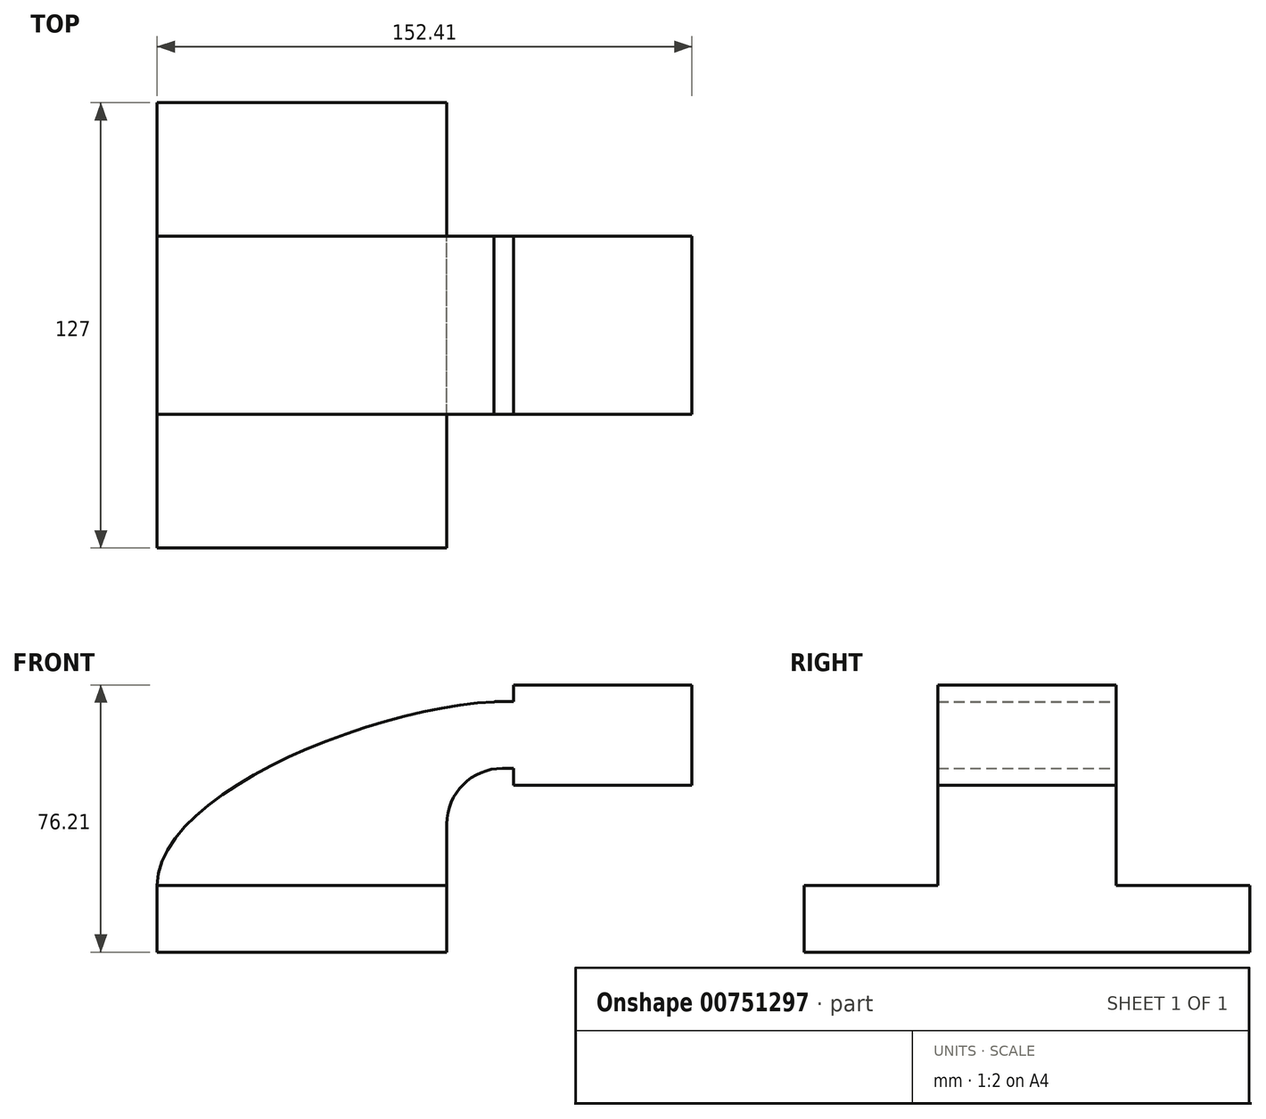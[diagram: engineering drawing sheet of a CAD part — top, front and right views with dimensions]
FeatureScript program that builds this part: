
annotation { "Feature Type Name" : "Feature", "Feature Type Description" : "" }
export const myFeature = defineFeature(function(context is Context, id is Id, definition is map)
    precondition{}
    {
        {
            var Q0;
            Q0=qCreatedBy(makeId("Front.planeOp"),FACE);
            var sketch = newSketch(context, id + "F0", { "sketchPlane" : qUnion([Q0])});
            skLineSegment(sketch, "E0.bottom", {"start": v(41.28, -9.52) * mm, "end": v(-41.28, -9.53) * mm});
            skLineSegment(sketch, "E0.top", {"start": v(41.28, 9.53) * mm, "end": v(-41.28, 9.53) * mm});
            skLineSegment(sketch, "E0.left", {"start": v(41.28, -9.52) * mm, "end": v(41.28, 9.53) * mm});
            skLineSegment(sketch, "E0.right", {"start": v(-41.28, -9.53) * mm, "end": v(-41.28, 9.53) * mm});
            skPoint(sketch, "E0.middle", {"position": v(0, 0) * mm});
            skLineSegment(sketch, "E1.bottom", {"start": v(111.12, 38.1) * mm, "end": v(60.32, 38.1) * mm});
            skLineSegment(sketch, "E1.top", {"start": v(111.12, 66.68) * mm, "end": v(60.32, 66.68) * mm});
            skLineSegment(sketch, "E1.left", {"start": v(111.12, 38.1) * mm, "end": v(111.12, 66.68) * mm});
            skLineSegment(sketch, "E1.right", {"start": v(60.32, 38.1) * mm, "end": v(60.32, 66.67) * mm});
            skPoint(sketch, "E1.middle", {"position": v(85.72, 52.39) * mm});
            skLineSegment(sketch, "E2", {"start": v(41.28, 9.53) * mm, "end": v(41.28, 27) * mm});
            skArc(sketch, "E3", {"start": v(41.27, 27) * mm, "mid": v(45.92, 38.23) * mm, "end": v(57.15, 42.88) * mm});
            skLineSegment(sketch, "E4", {"start": v(57.15, 42.88) * mm, "end": v(85.72, 42.88) * mm});
            skLineSegment(sketch, "E5.0", {"start": v(57.15, 61.93) * mm, "end": v(85.72, 61.93) * mm});
            skArc(sketch, "E5.1", {"start": v(22.23, 27) * mm, "mid": v(32.45, 51.7) * mm, "end": v(57.15, 61.93) * mm});
            skLineSegment(sketch, "E5.2", {"start": v(22.22, 9.53) * mm, "end": v(22.22, 27) * mm});
            skLineSegment(sketch, "E6", {"start": v(85.72, 38.1) * mm, "end": v(85.72, 66.68) * mm});
            skFitSpline(sketch, "E7", {"points": [v(-41.28, 9.53) * mm, v(57.15, 61.93) * mm], "startDerivative": vector(0.73, 80.71) * mm, "endDerivative": vector(103.58, 2.02) * mm});
            skSolve(sketch);
        }
        {
            var Q0;
            Q0=makeQuery(id+"F0.imprint","IMPRINT",FACE,{"disambiguationData":[TD([[makeQuery(id+"F0.imprint","IMPRINT",EDGE,{"derivedFrom":sQuery(id+"F0.wireOp",EDGE,"E0.bottom")}),-1.0]])]});
            extrude(context, id + "F1", {"entities" : qUnion([Q0]), "endBound" : BoundingType.SYMMETRIC, "depth" : 127 * mm, "offsetDistance" : 25.4 * mm});
        }
        {
            var Q0;
            Q0 = qSketchRegion(id + "F0", true);
            extrude(context, id + "F2", {"entities" : qUnion([Q0]), "operationType" : NewBodyOperationType.ADD, "endBound" : BoundingType.SYMMETRIC, "depth" : 50.8 * mm, "offsetDistance" : 25.4 * mm});
        }
    });
